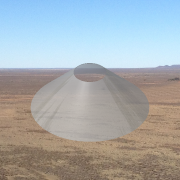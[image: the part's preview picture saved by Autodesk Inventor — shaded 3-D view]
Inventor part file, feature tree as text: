
AUTODESK INVENTOR PART (.ipt)
format: ipt  version: 2013 SP2 (Build 170200200, 200)  size: 156,672 bytes
history: native  units: in
note: dims shown in document units (in); Inventor stores cm internally (conversion verified against a paired STEP export)
features: sketch x2, revolve x1, plane x1, extrude x1
ambient origin geometry x8: Origin, YZ Plane, XZ Plane, XY Plane, X Axis, Y Axis, Z Axis, Center Point
bodies: Solid1 (feature_tree)
feature tree (5):
  revolve  "Revolution1"  Angle=45.0deg
  plane  "Work Plane1"
  extrude  "Extrusion2"  Depth=20.0in
  sketch  "Sketch1"  dims[d0=-0.0in d1=45.0deg]
  sketch  "Sketch5"  dims[d2=90.0deg d3=20.0in d7=10.0in d9=20.0in d10=0.0in]
